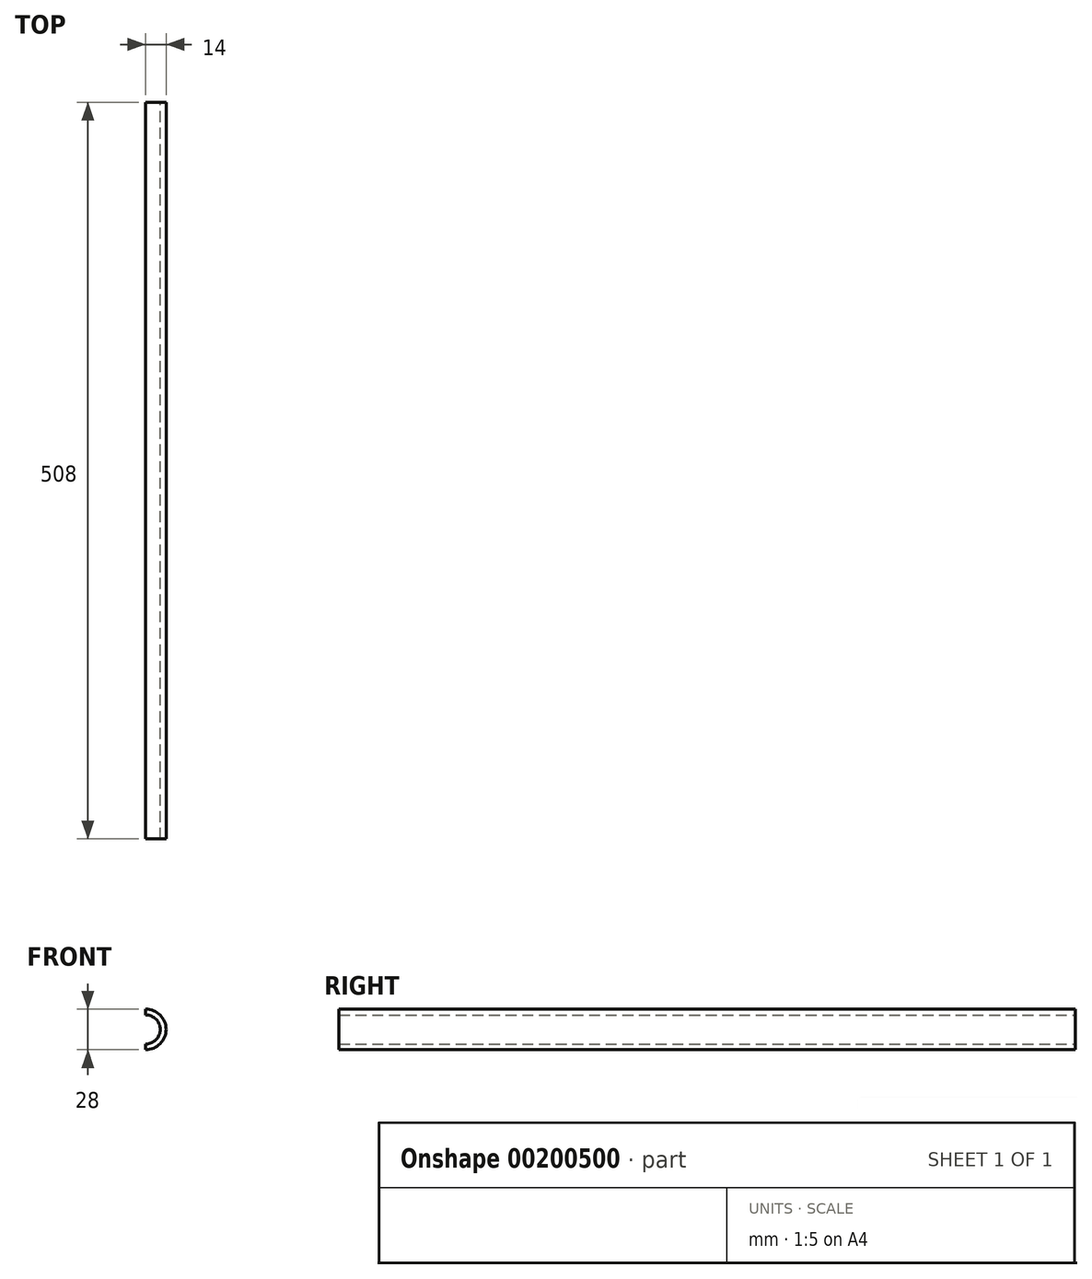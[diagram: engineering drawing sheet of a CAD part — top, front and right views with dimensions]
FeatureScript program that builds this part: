
annotation { "Feature Type Name" : "Feature", "Feature Type Description" : "" }
export const myFeature = defineFeature(function(context is Context, id is Id, definition is map)
    precondition{}
    {
        {
            var Q0;
            Q0=qCreatedBy(makeId("Front.planeOp"),FACE);
            var sketch = newSketch(context, id + "F0", { "sketchPlane" : qUnion([Q0])});
            skCircle(sketch, "E0", {"center": v(0, 0) * mm, "radius": 10 * mm});
            skCircle(sketch, "E1", {"center": v(0, 0) * mm, "radius": 14 * mm});
            skSolve(sketch);
        }
        {
            var Q0;
            Q0=makeQuery(id+"F0.imprint","IMPRINT",FACE,{"disambiguationData":[TD([[makeQuery(id+"F0.imprint","IMPRINT",EDGE,{"derivedFrom":sQuery(id+"F0.wireOp",EDGE,"E0")}),-1.0]])]});
            extrude(context, id + "F1", {"entities" : qUnion([Q0]), "depth" : 508 * mm});
        }
        {
            var Q0;
            Q0=qCreatedBy(makeId("Right.planeOp"),FACE);
            var sketch = newSketch(context, id + "F2", { "sketchPlane" : qUnion([Q0])});
            skLineSegment(sketch, "E2.bottom", {"start": v(12.7, 23.94) * mm, "end": v(-513.58, 23.94) * mm});
            skLineSegment(sketch, "E2.top", {"start": v(12.7, -30.27) * mm, "end": v(-513.58, -30.27) * mm});
            skLineSegment(sketch, "E2.left", {"start": v(12.7, 23.94) * mm, "end": v(12.7, -30.27) * mm});
            skLineSegment(sketch, "E2.right", {"start": v(-513.58, 23.94) * mm, "end": v(-513.58, -30.27) * mm});
            skSolve(sketch);
        }
        {
            var Q0;
            Q0=makeQuery(id+"F2.imprint","IMPRINT",FACE,{"disambiguationData":[TD([[makeQuery(id+"F2.imprint","IMPRINT",EDGE,{"derivedFrom":sQuery(id+"F2.wireOp",EDGE,"E2.bottom")}),1.0]])]});
            extrude(context, id + "F3", {"entities" : qUnion([Q0]), "operationType" : NewBodyOperationType.REMOVE, "oppositeDirection" : true, "depth" : 25.4 * mm});
        }
    });
